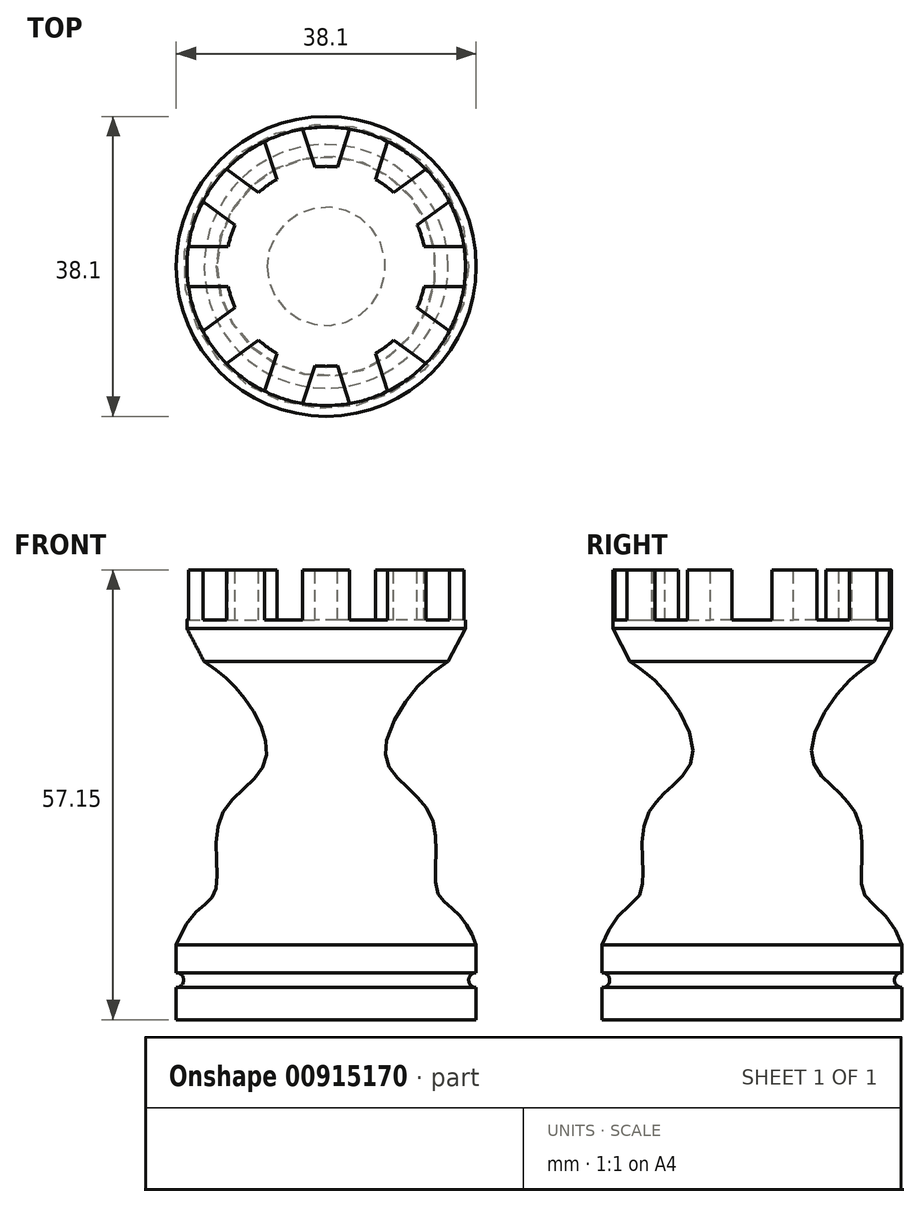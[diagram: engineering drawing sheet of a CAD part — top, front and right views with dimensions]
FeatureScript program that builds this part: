
annotation { "Feature Type Name" : "Feature", "Feature Type Description" : "" }
export const myFeature = defineFeature(function(context is Context, id is Id, definition is map)
    precondition{}
    {
        {
            var Q0;
            Q0=qCreatedBy(makeId("Front.planeOp"),FACE);
            var sketch = newSketch(context, id + "F0", { "sketchPlane" : qUnion([Q0])});
            skLineSegment(sketch, "E0", {"start": v(0, 0) * mm, "end": v(0, 57.15) * mm});
            skLineSegment(sketch, "E1", {"start": v(0, 0) * mm, "end": v(19.05, 0) * mm});
            skLineSegment(sketch, "E2", {"start": v(19.05, 0) * mm, "end": v(19.05, 9.53) * mm});
            skLineSegment(sketch, "E3", {"start": v(0, 47) * mm, "end": v(30.16, 47) * mm, "construction": true});
            skFitSpline(sketch, "E4", {"points": [v(19.05, 9.53) * mm, v(14.12, 16.22) * mm, v(13.35, 25.82) * mm, v(7.7, 32.86) * mm, v(10.87, 41.46) * mm, v(17.68, 47) * mm], "startDerivative": vector(-29.8, 78.75) * mm, "endDerivative": vector(49.06, 33.71) * mm});
            skLineSegment(sketch, "E5.bottom", {"start": v(0, 47) * mm, "end": v(17.68, 47) * mm});
            skLineSegment(sketch, "E5.top", {"start": v(0, 57.15) * mm, "end": v(17.68, 57.15) * mm});
            skLineSegment(sketch, "E5.left", {"start": v(0, 47) * mm, "end": v(0, 57.15) * mm});
            skLineSegment(sketch, "E5.right", {"start": v(17.68, 47) * mm, "end": v(17.68, 57.15) * mm});
            skSolve(sketch);
        }
        {
            var Q0;
            {var subQ2=sQuery(id+"F0.wireOp",EDGE,"E5.bottom");Q0=makeQuery(id+"F0.imprint","IMPRINT",FACE,{"disambiguationData":[TD([[makeQuery(id+"F0.imprint","IMPRINT",EDGE,{"derivedFrom":subQ2}),1.0]])]});}
            var Q1;
            {var subQ0=sQuery(id+"F0.wireOp",EDGE,"E1");Q1=makeQuery(id+"F0.imprint","IMPRINT",FACE,{"disambiguationData":[TD([[makeQuery(id+"F0.imprint","IMPRINT",EDGE,{"derivedFrom":subQ0}),1.0]])]});}
            var Q2;
            Q2=sQuery(id+"F0.wireOp",EDGE,"E0");
            revolve(context, id + "F1", {"surfaceOperationType" : NewSurfaceOperationType.NEW, "entities" : qUnion([Q0, Q1]), "axis" : qUnion([Q2]), "revolveType" : RevolveType.FULL});
        }
        {
            var Q0;
            Q0=makeQuery(id+"F1.opRevolve","SWEPT_FACE",FACE,{"disambiguationData":[OSD([sQuery(id+"F0.wireOp",EDGE,"E5.top")])]});
            var sketch = newSketch(context, id + "F2", { "sketchPlane" : qUnion([Q0])});
            skCircle(sketch, "E6", {"center": v(0, 0) * mm, "radius": 12.7 * mm});
            skSolve(sketch);
        }
        {
            var Q0;
            Q0=makeQuery(id+"F2.imprint","IMPRINT",FACE,{"disambiguationData":[TD([[makeQuery(id+"F2.imprint","IMPRINT",EDGE,{"derivedFrom":sQuery(id+"F2.wireOp",EDGE,"E6")}),1.0]])]});
            extrude(context, id + "F3", {"entities" : qUnion([Q0]), "operationType" : NewBodyOperationType.REMOVE, "oppositeDirection" : true, "depth" : 6.35 * mm, "offsetDistance" : 25.4 * mm});
        }
        {
            var Q0;
            Q0=makeQuery(id+"F1.opRevolve","SWEPT_FACE",FACE,{"disambiguationData":[OSD([sQuery(id+"F0.wireOp",EDGE,"E5.top")])]});
            var sketch = newSketch(context, id + "F4", { "sketchPlane" : qUnion([Q0])});
            skLineSegment(sketch, "E7", {"start": v(0, 0) * mm, "end": v(15.24, 0) * mm, "construction": true});
            skLineSegment(sketch, "E8.bottom", {"start": v(20.15, -2.54) * mm, "end": v(10.33, -2.54) * mm});
            skLineSegment(sketch, "E8.top", {"start": v(20.15, 2.54) * mm, "end": v(10.33, 2.54) * mm});
            skLineSegment(sketch, "E8.left", {"start": v(20.15, -2.54) * mm, "end": v(20.15, 2.54) * mm});
            skLineSegment(sketch, "E8.right", {"start": v(10.33, -2.54) * mm, "end": v(10.33, 2.54) * mm});
            skPoint(sketch, "E8.middle", {"position": v(15.24, 0) * mm});
            skLineSegment(sketch, "E9.1.0", {"start": v(9.85, 4.02) * mm, "end": v(6.86, 8.13) * mm});
            skLineSegment(sketch, "E9.1.1", {"start": v(17.8, 9.8) * mm, "end": v(14.81, 13.9) * mm});
            skPoint(sketch, "E9.1.2", {"position": v(12.33, 8.96) * mm});
            skLineSegment(sketch, "E9.1.3", {"start": v(17.8, 9.8) * mm, "end": v(9.85, 4.02) * mm});
            skLineSegment(sketch, "E9.1.4", {"start": v(14.81, 13.9) * mm, "end": v(6.86, 8.13) * mm});
            skLineSegment(sketch, "E9.2.0", {"start": v(5.6, 9.04) * mm, "end": v(0.78, 10.6) * mm});
            skLineSegment(sketch, "E9.2.1", {"start": v(8.64, 18.38) * mm, "end": v(3.81, 19.95) * mm});
            skPoint(sketch, "E9.2.2", {"position": v(4.7, 14.5) * mm});
            skLineSegment(sketch, "E9.2.3", {"start": v(8.64, 18.38) * mm, "end": v(5.6, 9.04) * mm});
            skLineSegment(sketch, "E9.2.4", {"start": v(3.81, 19.95) * mm, "end": v(0.78, 10.6) * mm});
            skLineSegment(sketch, "E9.3.0", {"start": v(-0.78, 10.6) * mm, "end": v(-5.6, 9.04) * mm});
            skLineSegment(sketch, "E9.3.1", {"start": v(-3.81, 19.95) * mm, "end": v(-8.64, 18.38) * mm});
            skPoint(sketch, "E9.3.2", {"position": v(-4.7, 14.5) * mm});
            skLineSegment(sketch, "E9.3.3", {"start": v(-3.81, 19.95) * mm, "end": v(-0.78, 10.6) * mm});
            skLineSegment(sketch, "E9.3.4", {"start": v(-8.64, 18.38) * mm, "end": v(-5.6, 9.04) * mm});
            skLineSegment(sketch, "E9.4.0", {"start": v(-6.86, 8.13) * mm, "end": v(-9.85, 4.02) * mm});
            skLineSegment(sketch, "E9.4.1", {"start": v(-14.81, 13.9) * mm, "end": v(-17.8, 9.8) * mm});
            skPoint(sketch, "E9.4.2", {"position": v(-12.33, 8.96) * mm});
            skLineSegment(sketch, "E9.4.3", {"start": v(-14.81, 13.9) * mm, "end": v(-6.86, 8.13) * mm});
            skLineSegment(sketch, "E9.4.4", {"start": v(-17.8, 9.8) * mm, "end": v(-9.85, 4.02) * mm});
            skLineSegment(sketch, "E9.5.0", {"start": v(-10.33, 2.54) * mm, "end": v(-10.33, -2.54) * mm});
            skLineSegment(sketch, "E9.5.1", {"start": v(-20.15, 2.54) * mm, "end": v(-20.15, -2.54) * mm});
            skPoint(sketch, "E9.5.2", {"position": v(-15.24, 0) * mm});
            skLineSegment(sketch, "E9.5.3", {"start": v(-20.15, 2.54) * mm, "end": v(-10.33, 2.54) * mm});
            skLineSegment(sketch, "E9.5.4", {"start": v(-20.15, -2.54) * mm, "end": v(-10.33, -2.54) * mm});
            skLineSegment(sketch, "E9.6.0", {"start": v(-9.85, -4.02) * mm, "end": v(-6.86, -8.13) * mm});
            skLineSegment(sketch, "E9.6.1", {"start": v(-17.8, -9.8) * mm, "end": v(-14.81, -13.9) * mm});
            skPoint(sketch, "E9.6.2", {"position": v(-12.33, -8.96) * mm});
            skLineSegment(sketch, "E9.6.3", {"start": v(-17.8, -9.8) * mm, "end": v(-9.85, -4.02) * mm});
            skLineSegment(sketch, "E9.6.4", {"start": v(-14.81, -13.9) * mm, "end": v(-6.86, -8.13) * mm});
            skLineSegment(sketch, "E9.7.0", {"start": v(-5.6, -9.04) * mm, "end": v(-0.78, -10.6) * mm});
            skLineSegment(sketch, "E9.7.1", {"start": v(-8.64, -18.38) * mm, "end": v(-3.81, -19.95) * mm});
            skPoint(sketch, "E9.7.2", {"position": v(-4.7, -14.5) * mm});
            skLineSegment(sketch, "E9.7.3", {"start": v(-8.64, -18.38) * mm, "end": v(-5.6, -9.04) * mm});
            skLineSegment(sketch, "E9.7.4", {"start": v(-3.81, -19.95) * mm, "end": v(-0.78, -10.6) * mm});
            skLineSegment(sketch, "E9.8.0", {"start": v(0.78, -10.6) * mm, "end": v(5.6, -9.04) * mm});
            skLineSegment(sketch, "E9.8.1", {"start": v(3.81, -19.95) * mm, "end": v(8.64, -18.38) * mm});
            skPoint(sketch, "E9.8.2", {"position": v(4.7, -14.5) * mm});
            skLineSegment(sketch, "E9.8.3", {"start": v(3.81, -19.95) * mm, "end": v(0.78, -10.6) * mm});
            skLineSegment(sketch, "E9.8.4", {"start": v(8.64, -18.38) * mm, "end": v(5.6, -9.04) * mm});
            skLineSegment(sketch, "E9.9.0", {"start": v(6.86, -8.13) * mm, "end": v(9.85, -4.02) * mm});
            skLineSegment(sketch, "E9.9.1", {"start": v(14.81, -13.9) * mm, "end": v(17.8, -9.8) * mm});
            skPoint(sketch, "E9.9.2", {"position": v(12.33, -8.96) * mm});
            skLineSegment(sketch, "E9.9.3", {"start": v(14.81, -13.9) * mm, "end": v(6.86, -8.13) * mm});
            skLineSegment(sketch, "E9.9.4", {"start": v(17.8, -9.8) * mm, "end": v(9.85, -4.02) * mm});
            skPoint(sketch, "E9.center", {"position": v(0, 0) * mm});
            skSolve(sketch);
        }
        {
            var Q0;
            Q0 = qSketchRegion(id + "F4", true);
            extrude(context, id + "F5", {"entities" : qUnion([Q0]), "operationType" : NewBodyOperationType.REMOVE, "oppositeDirection" : true, "depth" : 6.35 * mm, "offsetDistance" : 25.4 * mm});
        }
        {
            var Q0;
            Q0=makeQuery(id+"F1.opRevolve","SWEPT_EDGE",EDGE,{"disambiguationData":[OSD([sQuery(id+"F0.wireOp",EDGE,"E4"),sQuery(id+"F0.wireOp",EDGE,"E5.bottom"),sQuery(id+"F0.wireOp",EDGE,"E5.right")])]});
            chamfer(context, id + "F6", {"entities" : qUnion([Q0]), "width" : 5.08 * mm, "tangentPropagation" : true});
        }
        {
            var Q0;
            Q0=qCreatedBy(makeId("Front.planeOp"),FACE);
            var sketch = newSketch(context, id + "F7", { "sketchPlane" : qUnion([Q0])});
            skLineSegment(sketch, "E10", {"start": v(0, 0) * mm, "end": v(0, 10.06) * mm, "construction": true});
            skLineSegment(sketch, "E11", {"start": v(0, 5.03) * mm, "end": v(19.03, 5.03) * mm, "construction": true});
            skCircle(sketch, "E12", {"center": v(19.03, 5.03) * mm, "radius": 0.94 * mm});
            skSolve(sketch);
        }
        {
            var Q0;
            Q0 = qSketchRegion(id + "F7", true);
            var Q1;
            Q1 = qConstructionFilter(qBodyType(qCreatedBy(id + "F7" ,EDGE), BodyType.WIRE), ConstructionObject.NO);
            var Q2;
            Q2=sQuery(id+"F7.wireOp",EDGE,"E10");
            revolve(context, id + "F8", {"operationType" : NewBodyOperationType.REMOVE, "surfaceOperationType" : NewSurfaceOperationType.ADD, "entities" : qUnion([Q0]), "surfaceEntities" : qUnion([Q1]), "axis" : qUnion([Q2]), "revolveType" : RevolveType.FULL, "oppositeDirection" : true});
        }
    });
